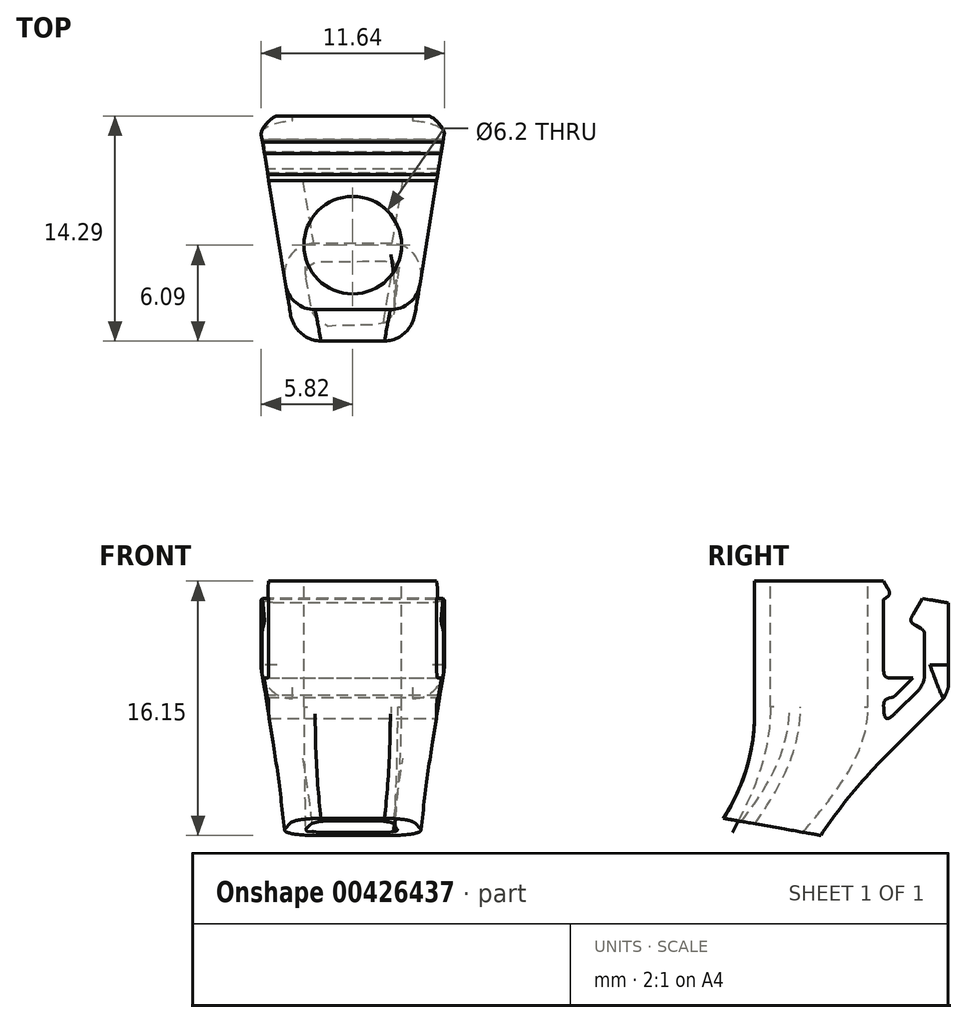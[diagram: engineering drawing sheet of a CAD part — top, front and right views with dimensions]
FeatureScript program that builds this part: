
annotation { "Feature Type Name" : "Feature", "Feature Type Description" : "" }
export const myFeature = defineFeature(function(context is Context, id is Id, definition is map)
    precondition{}
    {
        {
            var Q0;
            Q0=qCreatedBy(makeId("Right.planeOp"),FACE);
            var sketch = newSketch(context, id + "F0", { "sketchPlane" : qUnion([Q0])});
            skLineSegment(sketch, "E0", {"start": v(0, 0) * mm, "end": v(7, 0) * mm});
            skLineSegment(sketch, "E1", {"start": v(15.1, 9) * mm, "end": v(15.1, 14.77) * mm});
            skLineSegment(sketch, "E2", {"start": v(13.45, 15.06) * mm, "end": v(12.6, 13.58) * mm});
            skLineSegment(sketch, "E3", {"start": v(12.6, 13.58) * mm, "end": v(13.6, 13) * mm});
            skLineSegment(sketch, "E4", {"start": v(13.6, 13) * mm, "end": v(13.6, 10) * mm});
            skLineSegment(sketch, "E5", {"start": v(13.6, 10) * mm, "end": v(11, 10) * mm});
            skLineSegment(sketch, "E6", {"start": v(11, 10) * mm, "end": v(11, 15) * mm});
            skLineSegment(sketch, "E7", {"start": v(11, 15) * mm, "end": v(11.5, 15.29) * mm});
            skLineSegment(sketch, "E8", {"start": v(11.5, 15.29) * mm, "end": v(11, 16.15) * mm});
            skLineSegment(sketch, "E9", {"start": v(11, 16.15) * mm, "end": v(2.8, 16.15) * mm});
            skLineSegment(sketch, "E10", {"start": v(2.8, 16.15) * mm, "end": v(0, 0) * mm, "construction": true});
            skLineSegment(sketch, "E11", {"start": v(2.8, 16.15) * mm, "end": v(2.8, 7.7) * mm});
            skArc(sketch, "E12", {"start": v(0, 0) * mm, "mid": v(2.08, 3.6) * mm, "end": v(2.8, 7.7) * mm});
            skLineSegment(sketch, "E13", {"start": v(15.1, 9) * mm, "end": v(11, 4.9) * mm});
            skArc(sketch, "E14", {"start": v(7, 0) * mm, "mid": v(8.88, 2.54) * mm, "end": v(11, 4.9) * mm});
            skLineSegment(sketch, "E15", {"start": v(13.45, 15.06) * mm, "end": v(15.1, 14.77) * mm});
            skSolve(sketch);
        }
        {
            var Q0;
            Q0 = qSketchRegion(id + "F0", true);
            extrude(context, id + "F1", {"entities" : qUnion([Q0]), "endBound" : BoundingType.SYMMETRIC, "depth" : 12 * mm});
        }
        {
            var Q0;
            Q0=qCreatedBy(makeId("Right.planeOp"),FACE);
            var sketch = newSketch(context, id + "F2", { "sketchPlane" : qUnion([Q0])});
            skLineSegment(sketch, "E16", {"start": v(13.6, 9.62) * mm, "end": v(11, 7.02) * mm});
            skLineSegment(sketch, "E17", {"start": v(11, 7.02) * mm, "end": v(11, 8.63) * mm});
            skLineSegment(sketch, "E18", {"start": v(11, 8.63) * mm, "end": v(11.65, 8.8) * mm});
            skLineSegment(sketch, "E19", {"start": v(11.65, 8.8) * mm, "end": v(12.85, 10) * mm});
            skLineSegment(sketch, "E20", {"start": v(12.85, 10) * mm, "end": v(13.6, 10) * mm});
            skLineSegment(sketch, "E21", {"start": v(13.6, 9.62) * mm, "end": v(13.6, 10) * mm});
            skSolve(sketch);
        }
        {
            var Q0;
            Q0 = qSketchRegion(id + "F2", true);
            extrude(context, id + "F3", {"entities" : qUnion([Q0]), "operationType" : NewBodyOperationType.REMOVE, "endBound" : BoundingType.THROUGH_ALL, "oppositeDirection" : true, "depth" : 25 * mm, "hasSecondDirection" : true, "secondDirectionBound" : SecondDirectionBoundingType.THROUGH_ALL, "secondDirectionOppositeDirection" : false, "secondDirectionDepth" : 25 * mm});
        }
        {
            var Q0;
            Q0=makeQuery(id+"F1.opExtrude","SWEPT_FACE",FACE,{"disambiguationData":[OSD([sQuery(id+"F0.wireOp",EDGE,"E9")])]});
            var sketch = newSketch(context, id + "F4", { "sketchPlane" : qUnion([Q0])});
            skLineSegment(sketch, "E22", {"start": v(-6, 15.1) * mm, "end": v(-4, 2.8) * mm});
            skLineSegment(sketch, "E23", {"start": v(-4, 2.8) * mm, "end": v(-6, 2.8) * mm});
            skLineSegment(sketch, "E24", {"start": v(-6, 2.8) * mm, "end": v(-6, 15.1) * mm});
            skLineSegment(sketch, "E25", {"start": v(6, 2.8) * mm, "end": v(4, 2.8) * mm});
            skLineSegment(sketch, "E26", {"start": v(4, 2.8) * mm, "end": v(6, 15.1) * mm});
            skLineSegment(sketch, "E27", {"start": v(6, 15.1) * mm, "end": v(6, 2.8) * mm});
            skLineSegment(sketch, "E28", {"start": v(-4, 2.8) * mm, "end": v(-3.54, 0) * mm});
            skLineSegment(sketch, "E29", {"start": v(-3.54, 0) * mm, "end": v(-6, 0) * mm});
            skLineSegment(sketch, "E30", {"start": v(-6, 0) * mm, "end": v(-6, 2.8) * mm});
            skLineSegment(sketch, "E31", {"start": v(6, 2.8) * mm, "end": v(6, 0) * mm});
            skLineSegment(sketch, "E32", {"start": v(6, 0) * mm, "end": v(3.54, 0) * mm});
            skLineSegment(sketch, "E33", {"start": v(3.54, 0) * mm, "end": v(4, 2.8) * mm});
            skSolve(sketch);
        }
        {
            var Q0;
            Q0 = qSketchRegion(id + "F4", true);
            extrude(context, id + "F5", {"entities" : qUnion([Q0]), "operationType" : NewBodyOperationType.REMOVE, "endBound" : BoundingType.THROUGH_ALL, "oppositeDirection" : true, "depth" : 25 * mm});
        }
        {
            var Q0;
            Q0=makeQuery(id+"F5.boolean.opBoolean","INTERSECT",EDGE,{"derivedFrom":[makeQuery(id+"F1.opExtrude","SWEPT_FACE",FACE,{"disambiguationData":[OSD([sQuery(id+"F0.wireOp",EDGE,"E14")])]}),makeQuery(id+"F5.opExtrude","SWEPT_FACE",FACE,{"disambiguationData":[OSD([sQuery(id+"F4.wireOp",EDGE,"E22"),sQuery(id+"F4.wireOp",EDGE,"E28")])]})]});
            var Q1;
            Q1=makeQuery(id+"F5.boolean.opBoolean","INTERSECT",EDGE,{"derivedFrom":[makeQuery(id+"F1.opExtrude","SWEPT_FACE",FACE,{"disambiguationData":[OSD([sQuery(id+"F0.wireOp",EDGE,"E12")])]}),makeQuery(id+"F5.opExtrude","SWEPT_FACE",FACE,{"disambiguationData":[OSD([sQuery(id+"F4.wireOp",EDGE,"E22"),sQuery(id+"F4.wireOp",EDGE,"E28")])]})]});
            var Q2;
            Q2=makeQuery(id+"F5.boolean.opBoolean","INTERSECT",EDGE,{"derivedFrom":[makeQuery(id+"F1.opExtrude","SWEPT_FACE",FACE,{"disambiguationData":[OSD([sQuery(id+"F0.wireOp",EDGE,"E14")])]}),makeQuery(id+"F5.opExtrude","SWEPT_FACE",FACE,{"disambiguationData":[OSD([sQuery(id+"F4.wireOp",EDGE,"E26"),sQuery(id+"F4.wireOp",EDGE,"E33")])]})]});
            var Q3;
            Q3=makeQuery(id+"F5.boolean.opBoolean","INTERSECT",EDGE,{"derivedFrom":[makeQuery(id+"F1.opExtrude","SWEPT_FACE",FACE,{"disambiguationData":[OSD([sQuery(id+"F0.wireOp",EDGE,"E12")])]}),makeQuery(id+"F5.opExtrude","SWEPT_FACE",FACE,{"disambiguationData":[OSD([sQuery(id+"F4.wireOp",EDGE,"E26"),sQuery(id+"F4.wireOp",EDGE,"E33")])]})]});
            fillet(context, id + "F6", {"entities" : qUnion([Q0, Q1, Q2, Q3]), "radius" : 1.9 * mm, "tangentPropagation" : true, "allowEdgeOverflow" : false});
        }
        {
            var Q0;
            Q0=makeQuery(id+"F1.opExtrude","SWEPT_FACE",FACE,{"disambiguationData":[OSD([sQuery(id+"F0.wireOp",EDGE,"E0")])]});
            var sketch = newSketch(context, id + "F7", { "sketchPlane" : qUnion([Q0])});
            skFitSpline(sketch, "E34.0", {"points": [v(-2.98, -4.65) * mm, v(-3, -4.72) * mm, v(-3, -4.83) * mm, v(-3, -4.98) * mm, v(-2.98, -5.12) * mm, v(-2.93, -5.3) * mm, v(-2.87, -5.43) * mm, v(-2.8, -5.53) * mm, v(-2.74, -5.6) * mm, v(-2.65, -5.66) * mm, v(-2.58, -5.7) * mm, v(-2.53, -5.7) * mm, v(-2.5, -5.7) * mm]});
            skLineSegment(sketch, "E34.1", {"start": v(2.5, -5.7) * mm, "end": v(-2.5, -5.7) * mm});
            skLineSegment(sketch, "E34.2", {"start": v(-2.98, -4.65) * mm, "end": v(-2.6, -2.27) * mm});
            skFitSpline(sketch, "E34.3", {"points": [v(2.5, -5.7) * mm, v(2.53, -5.7) * mm, v(2.56, -5.7) * mm, v(2.62, -5.68) * mm, v(2.67, -5.65) * mm, v(2.75, -5.58) * mm, v(2.88, -5.42) * mm, v(3, -5.1) * mm, v(3, -4.8) * mm, v(2.98, -4.65) * mm]});
            skFitSpline(sketch, "E34.4", {"points": [v(-1.84, -1.3) * mm, v(-1.85, -1.3) * mm, v(-1.88, -1.3) * mm, v(-1.96, -1.33) * mm, v(-2.04, -1.38) * mm, v(-2.13, -1.45) * mm, v(-2.25, -1.56) * mm, v(-2.38, -1.74) * mm, v(-2.52, -2) * mm, v(-2.59, -2.22) * mm, v(-2.61, -2.37) * mm]});
            skLineSegment(sketch, "E34.5", {"start": v(1.86, -1.3) * mm, "end": v(-1.86, -1.3) * mm});
            skFitSpline(sketch, "E34.6", {"points": [v(2.61, -2.37) * mm, v(2.6, -2.3) * mm, v(2.57, -2.15) * mm, v(2.49, -1.94) * mm, v(2.37, -1.73) * mm, v(2.25, -1.57) * mm, v(2.1, -1.43) * mm, v(1.98, -1.34) * mm, v(1.87, -1.3) * mm, v(1.85, -1.3) * mm, v(1.84, -1.3) * mm]});
            skLineSegment(sketch, "E34.7", {"start": v(2.6, -2.27) * mm, "end": v(2.98, -4.65) * mm});
            skSolve(sketch);
        }
        {
            var Q0;
            Q0=makeQuery(id+"F1.opExtrude","SWEPT_FACE",FACE,{"disambiguationData":[OSD([sQuery(id+"F0.wireOp",EDGE,"E9")])]});
            var sketch = newSketch(context, id + "F8", { "sketchPlane" : qUnion([Q0])});
            skLineSegment(sketch, "E35", {"start": v(0, 11) * mm, "end": v(0, 11) * mm});
            skCircle(sketch, "E36", {"center": v(0, 6.9) * mm, "radius": 3.1 * mm});
            skLineSegment(sketch, "E37", {"start": v(0, 11) * mm, "end": v(0, 10) * mm, "construction": true});
            skLineSegment(sketch, "E38", {"start": v(0, 10) * mm, "end": v(0, 10) * mm});
            skLineSegment(sketch, "E39", {"start": v(0, 2.8) * mm, "end": v(0, 3.8) * mm, "construction": true});
            skSolve(sketch);
        }
        {
            var Q0;
            Q0=makeQuery(id+"F8.imprint","IMPRINT",FACE,{"disambiguationData":[TD([[makeQuery(id+"F8.imprint","IMPRINT",EDGE,{"derivedFrom":sQuery(id+"F8.wireOp",EDGE,"E36")}),1.0]])]});
            var Q1;
            Q1=sQuery(id+"F8.wireOp",EDGE,"E36");
            extrude(context, id + "F9", {"entities" : qUnion([Q0]), "operationType" : NewBodyOperationType.REMOVE, "surfaceEntities" : qUnion([Q1]), "oppositeDirection" : true, "depth" : 8 * mm});
        }
        {
            var Q0;
            Q0=makeQuery(id+"F9.boolean.opBoolean","COPY",FACE,{"derivedFrom":makeQuery(id+"F9.opExtrude","CAP_FACE",FACE,{"disambiguationData":[OSD([sQuery(id+"F8.wireOp",EDGE,"E36")])],"isStart":false})});
            var sketch = newSketch(context, id + "F10", { "sketchPlane" : qUnion([Q0])});
            skArc(sketch, "E40", {"start": v(1.19, 9.76) * mm, "mid": v(0, 10) * mm, "end": v(-1.19, 9.76) * mm});
            skLineSegment(sketch, "E41", {"start": v(-1.19, 9.76) * mm, "end": v(0, 6.9) * mm, "construction": true});
            skLineSegment(sketch, "E42", {"start": v(0, 6.9) * mm, "end": v(1.19, 9.76) * mm, "construction": true});
            skLineSegment(sketch, "E43", {"start": v(0, 6.9) * mm, "end": v(0, 10) * mm, "construction": true});
            skArc(sketch, "E44.1.0", {"start": v(-1.19, 9.76) * mm, "mid": v(-2.2, 9.1) * mm, "end": v(-2.86, 8.09) * mm});
            skArc(sketch, "E44.2.0", {"start": v(-2.86, 8.09) * mm, "mid": v(-3.1, 6.9) * mm, "end": v(-2.86, 5.71) * mm});
            skArc(sketch, "E44.3.0", {"start": v(-2.86, 5.71) * mm, "mid": v(-2.2, 4.7) * mm, "end": v(-1.19, 4.04) * mm});
            skArc(sketch, "E44.4.0", {"start": v(-1.19, 4.04) * mm, "mid": v(0, 3.8) * mm, "end": v(1.19, 4.04) * mm});
            skArc(sketch, "E44.5.0", {"start": v(1.19, 4.04) * mm, "mid": v(2.2, 4.7) * mm, "end": v(2.86, 5.71) * mm});
            skArc(sketch, "E44.6.0", {"start": v(2.86, 5.71) * mm, "mid": v(3.1, 6.9) * mm, "end": v(2.86, 8.09) * mm});
            skArc(sketch, "E44.7.0", {"start": v(2.86, 8.09) * mm, "mid": v(2.2, 9.1) * mm, "end": v(1.19, 9.76) * mm});
            skSolve(sketch);
        }
        {
            var Q1;
            Q1 = qSketchRegion(id + "F7", true);
            var Q2;
            Q2 = qSketchRegion(id + "F10", true);
            loft(context, id + "F11", {"operationType" : NewBodyOperationType.REMOVE, "endCondition" : LoftEndDerivativeType.NORMAL_TO_PROFILE, "endMagnitude" : 1.2, "sheetProfilesArray" : [{ "sheetProfileEntities" : qUnion([Q1]) }, { "sheetProfileEntities" : qUnion([Q2]) }]});
        }
        {
            var Q0;
            Q0=makeQuery(id+"F5.boolean.opBoolean","MERGE",EDGE,{"derivedFrom":[makeQuery(id+"F1.opExtrude","CAP_EDGE",EDGE,{"disambiguationData":[OSD([sQuery(id+"F0.wireOp",EDGE,"E1")])],"isStart":true}),makeQuery(id+"F5.opExtrude","SWEPT_EDGE",EDGE,{"disambiguationData":[OSD([sQuery(id+"F4.wireOp",EDGE,"E22"),sQuery(id+"F4.wireOp",EDGE,"E24")])]})]});
            fillet(context, id + "F12", {"entities" : qUnion([Q0]), "radius" : 1 * mm, "tangentPropagation" : true, "rho" : .2, "crossSection" : FilletCrossSection.CONIC, "allowEdgeOverflow" : false});
        }
        {
            var Q0;
            Q0=makeQuery(id+"F3.boolean.opBoolean","COPY",EDGE,{"derivedFrom":makeQuery(id+"F3.opExtrude","SWEPT_EDGE",EDGE,{"disambiguationData":[OSD([sQuery(id+"F2.wireOp",EDGE,"E16"),sQuery(id+"F2.wireOp",EDGE,"E17")])]})});
            var Q1;
            Q1=makeQuery(id+"F3.boolean.opBoolean","COPY",EDGE,{"derivedFrom":makeQuery(id+"F3.opExtrude","SWEPT_EDGE",EDGE,{"disambiguationData":[OSD([sQuery(id+"F2.wireOp",EDGE,"E17"),sQuery(id+"F2.wireOp",EDGE,"E18")])]})});
            var Q2;
            Q2=makeQuery(id+"F3.boolean.opBoolean","COPY",EDGE,{"derivedFrom":makeQuery(id+"F3.opExtrude","SWEPT_EDGE",EDGE,{"disambiguationData":[OSD([sQuery(id+"F2.wireOp",EDGE,"E18"),sQuery(id+"F2.wireOp",EDGE,"E19")])]})});
            var Q3;
            Q3=makeQuery(id+"F3.boolean.opBoolean","COPY",EDGE,{"derivedFrom":makeQuery(id+"F3.opExtrude","SWEPT_EDGE",EDGE,{"disambiguationData":[OSD([sQuery(id+"F2.wireOp",EDGE,"E19"),sQuery(id+"F2.wireOp",EDGE,"E20")])]})});
            var Q4;
            Q4=makeQuery(id+"F1.opExtrude","SWEPT_EDGE",EDGE,{"disambiguationData":[OSD([sQuery(id+"F0.wireOp",EDGE,"E5"),sQuery(id+"F0.wireOp",EDGE,"E6")])]});
            var Q5;
            Q5=makeQuery(id+"F1.opExtrude","SWEPT_EDGE",EDGE,{"disambiguationData":[OSD([sQuery(id+"F0.wireOp",EDGE,"E2"),sQuery(id+"F0.wireOp",EDGE,"E3")])]});
            var Q6;
            Q6=makeQuery(id+"F1.opExtrude","SWEPT_EDGE",EDGE,{"disambiguationData":[OSD([sQuery(id+"F0.wireOp",EDGE,"E3"),sQuery(id+"F0.wireOp",EDGE,"E4")])]});
            var Q7;
            Q7=makeQuery(id+"F1.opExtrude","SWEPT_EDGE",EDGE,{"disambiguationData":[OSD([sQuery(id+"F0.wireOp",EDGE,"E7"),sQuery(id+"F0.wireOp",EDGE,"E8")])]});
            fillet(context, id + "F13", {"entities" : qUnion([Q0, Q1, Q2, Q3, Q4, Q5, Q6, Q7]), "radius" : .5 * mm, "tangentPropagation" : true, "rho" : .6, "crossSection" : FilletCrossSection.CONIC, "allowEdgeOverflow" : false});
        }
        {
            var Q0;
            Q0=makeQuery(id+"F3.boolean.opBoolean","COPY",EDGE,{"derivedFrom":makeQuery(id+"F3.opExtrude","SWEPT_EDGE",EDGE,{"disambiguationData":[OSD([sQuery(id+"F2.wireOp",EDGE,"E16"),sQuery(id+"F2.wireOp",EDGE,"E21")])]})});
            fillet(context, id + "F14", {"entities" : qUnion([Q0]), "radius" : 1.5 * mm, "tangentPropagation" : true, "allowEdgeOverflow" : false});
        }
        {
            var Q0;
            Q0=qCreatedBy(makeId("Right.planeOp"),FACE);
            var sketch = newSketch(context, id + "F15", { "sketchPlane" : qUnion([Q0])});
            skLineSegment(sketch, "E45", {"start": v(7, 0) * mm, "end": v(0, 0) * mm});
            skLineSegment(sketch, "E46", {"start": v(0, 0) * mm, "end": v(0, 1.23) * mm});
            skLineSegment(sketch, "E47", {"start": v(0, 1.23) * mm, "end": v(7, 0) * mm});
            skSolve(sketch);
        }
        {
            var Q0;
            Q0 = qSketchRegion(id + "F15", true);
            extrude(context, id + "F16", {"entities" : qUnion([Q0]), "operationType" : NewBodyOperationType.REMOVE, "endBound" : BoundingType.THROUGH_ALL, "oppositeDirection" : true, "depth" : 25 * mm, "hasSecondDirection" : true, "secondDirectionBound" : SecondDirectionBoundingType.THROUGH_ALL, "secondDirectionOppositeDirection" : false, "secondDirectionDepth" : 25 * mm});
        }
    });
